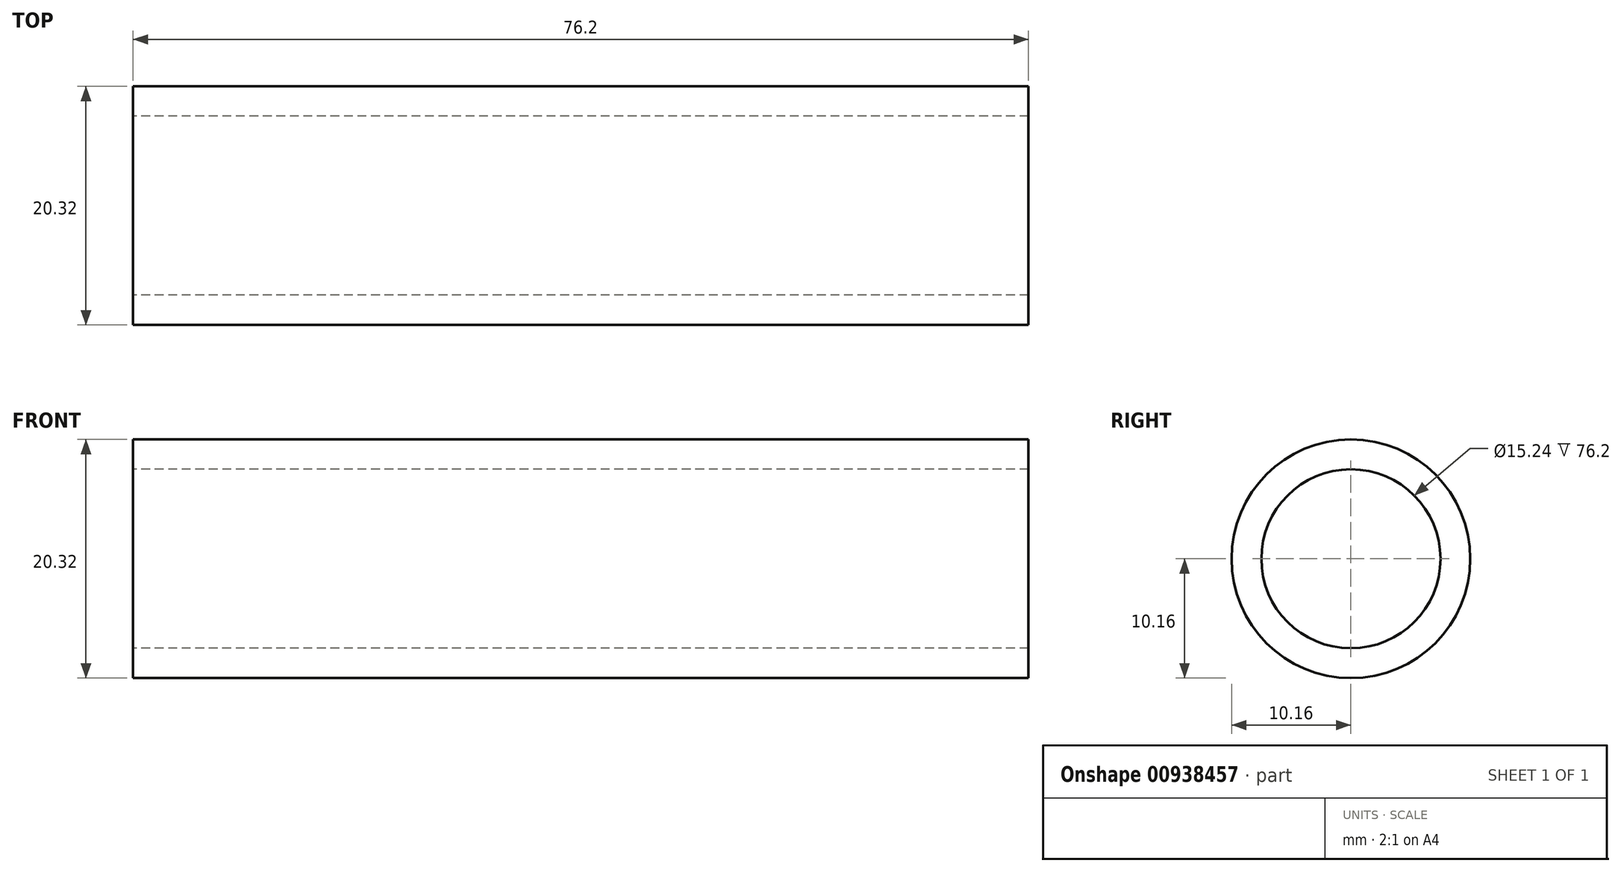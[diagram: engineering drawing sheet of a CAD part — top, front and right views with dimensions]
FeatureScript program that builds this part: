
annotation { "Feature Type Name" : "Feature", "Feature Type Description" : "" }
export const myFeature = defineFeature(function(context is Context, id is Id, definition is map)
    precondition{}
    {
        {
            var Q0;
            Q0=qCreatedBy(makeId("Right.planeOp"),FACE);
            var sketch = newSketch(context, id + "F0", { "sketchPlane" : qUnion([Q0])});
            skCircle(sketch, "E0", {"center": v(0, 0) * mm, "radius": 10.16 * mm});
            skSolve(sketch);
        }
        {
            var Q0;
            Q0=makeQuery(id+"F0.imprint","IMPRINT",FACE,{"disambiguationData":[TD([[makeQuery(id+"F0.imprint","IMPRINT",EDGE,{"derivedFrom":sQuery(id+"F0.wireOp",EDGE,"E0")}),1.0]])]});
            extrude(context, id + "F1", {"entities" : qUnion([Q0]), "depth" : 76.2 * mm, "offsetDistance" : 25.4 * mm});
        }
        {
            var Q0;
            Q0=qCreatedBy(makeId("Right.planeOp"),FACE);
            var sketch = newSketch(context, id + "F2", { "sketchPlane" : qUnion([Q0])});
            skCircle(sketch, "E1", {"center": v(0, 0) * mm, "radius": 7.62 * mm});
            skSolve(sketch);
        }
        {
            var Q0;
            Q0=makeQuery(id+"F2.imprint","IMPRINT",FACE,{"disambiguationData":[TD([[makeQuery(id+"F2.imprint","IMPRINT",EDGE,{"derivedFrom":sQuery(id+"F2.wireOp",EDGE,"E1")}),1.0]])]});
            var Q1;
            Q1=sQuery(id+"F2.wireOp",EDGE,"E1");
            extrude(context, id + "F3", {"entities" : qUnion([Q0]), "operationType" : NewBodyOperationType.REMOVE, "surfaceEntities" : qUnion([Q1]), "depth" : 76.2 * mm, "offsetDistance" : 25.4 * mm});
        }
    });
